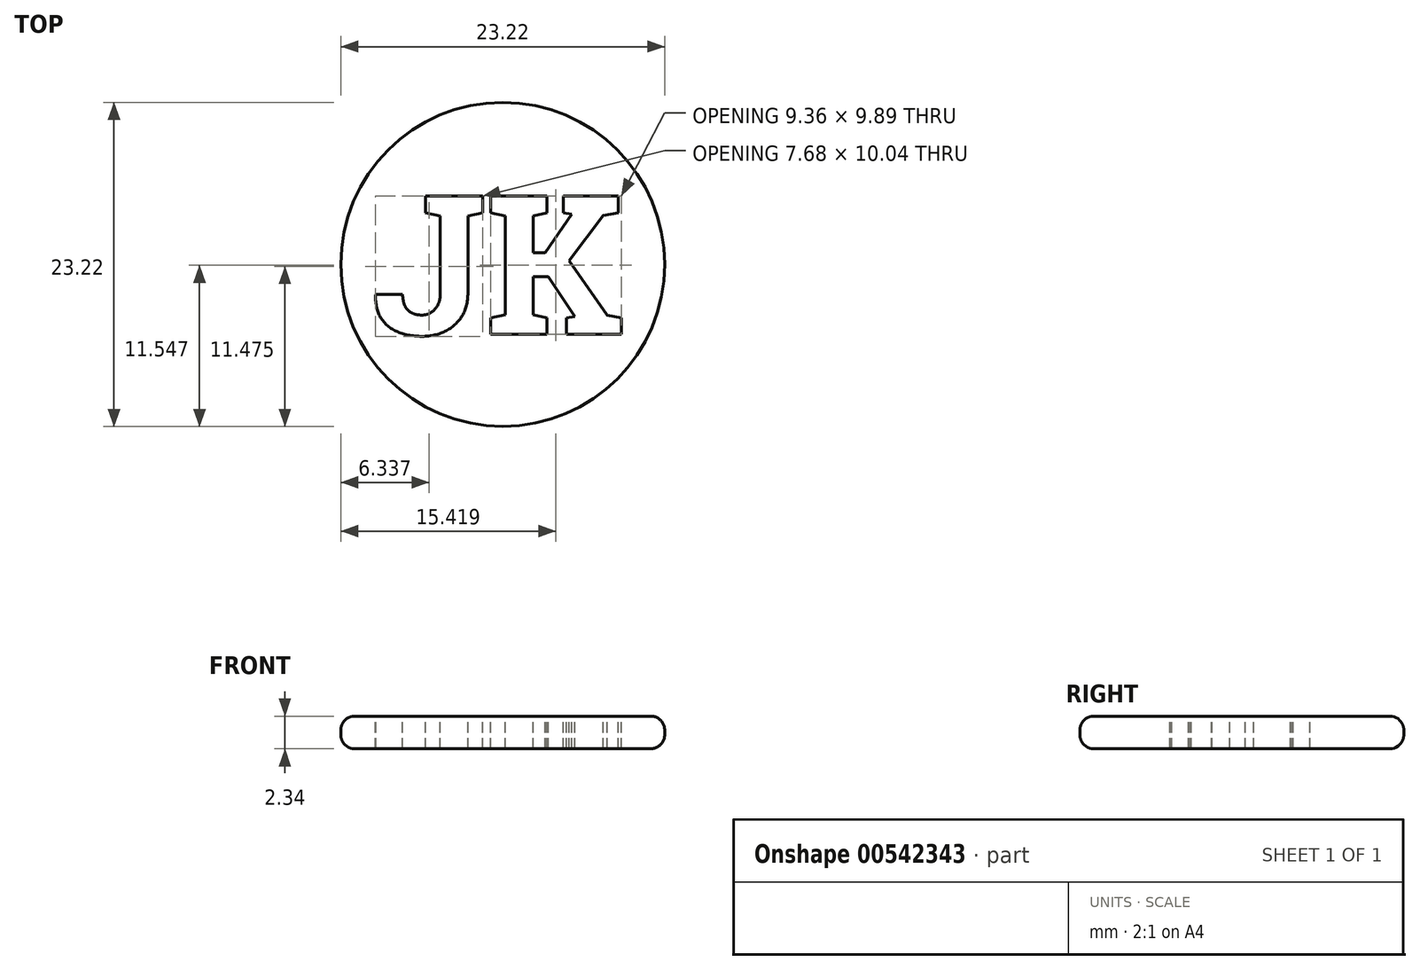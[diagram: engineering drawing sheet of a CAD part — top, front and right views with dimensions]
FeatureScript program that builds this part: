
annotation { "Feature Type Name" : "Feature", "Feature Type Description" : "" }
export const myFeature = defineFeature(function(context is Context, id is Id, definition is map)
    precondition{}
    {
        {
            var Q0;
            Q0=qCreatedBy(makeId("Top.planeOp"),FACE);
            var sketch = newSketch(context, id + "F0", { "sketchPlane" : qUnion([Q0])});
            skCircle(sketch, "E0", {"center": v(0, 0) * mm, "radius": 11.6 * mm});
            skSolve(sketch);
        }
        {
            var Q0;
            Q0 = qSketchRegion(id + "F0", true);
            extrude(context, id + "F1", {"entities" : qUnion([Q0]), "endBound" : BoundingType.SYMMETRIC, "depth" : 2.33 * mm, "offsetDistance" : 25 * mm});
        }
        {
            var Q0;
            Q0=makeQuery(id+"F1.opExtrude","CAP_EDGE",EDGE,{"disambiguationData":[OSD([sQuery(id+"F0.wireOp",EDGE,"E0")])],"isStart":false});
            var Q1;
            Q1=makeQuery(id+"F1.opExtrude","CAP_EDGE",EDGE,{"disambiguationData":[OSD([sQuery(id+"F0.wireOp",EDGE,"E0")])],"isStart":true});
            fillet(context, id + "F2", {"entities" : qUnion([Q0, Q1]), "radius" : 1 * mm, "tangentPropagation" : true, "allowEdgeOverflow" : false});
        }
        {
            var Q0;
            Q0=makeQuery(id+"F1.opExtrude","CAP_FACE",FACE,{"disambiguationData":[OSD([sQuery(id+"F0.wireOp",EDGE,"E0")])],"isStart":false});
            var sketch = newSketch(context, id + "F3", { "sketchPlane" : qUnion([Q0])});
            skText(sketch, "E1", { "text": "JK", "fontName": "RobotoSlab-Bold.ttf"});
            const initialGuessF3  = {"E1": [-0.00935, -0.00501, 1, 0, 0.01002]};
            skSetInitialGuess(sketch, initialGuessF3);
            skSolve(sketch);
        }
        {
            var Q0;
            Q0=makeQuery(id+"F3.imprint","IMPRINT",FACE,{"disambiguationData":[TD([[makeQuery(id+"F3.imprint","IMPRINT",EDGE,{"derivedFrom":sQuery(id+"F3.wireOp",EDGE,"E1.sketch_text.stroke-0")}),-1.0]])]});
            var Q1;
            Q1=makeQuery(id+"F3.imprint","IMPRINT",FACE,{"disambiguationData":[TD([[makeQuery(id+"F3.imprint","IMPRINT",EDGE,{"derivedFrom":sQuery(id+"F3.wireOp",EDGE,"E1.sketch_text.stroke-18")}),-1.0]])]});
            extrude(context, id + "F4", {"entities" : qUnion([Q0, Q1]), "operationType" : NewBodyOperationType.REMOVE, "endBound" : BoundingType.THROUGH_ALL, "oppositeDirection" : true, "depth" : 25 * mm, "offsetDistance" : 25 * mm});
        }
    });
